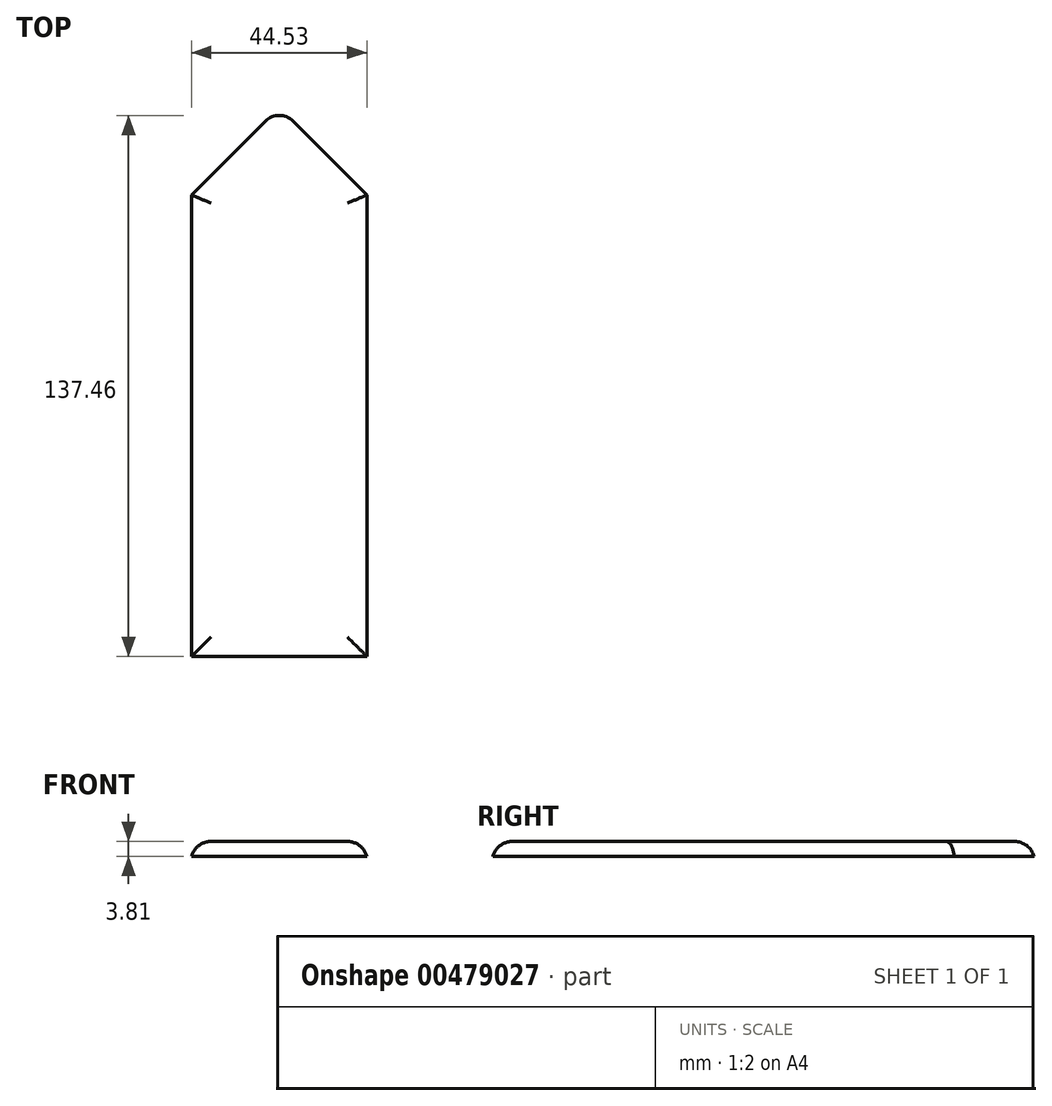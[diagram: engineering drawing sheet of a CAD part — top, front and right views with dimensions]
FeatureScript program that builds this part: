
annotation { "Feature Type Name" : "Feature", "Feature Type Description" : "" }
export const myFeature = defineFeature(function(context is Context, id is Id, definition is map)
    precondition{}
    {
        {
            var Q0;
            Q0=qCreatedBy(makeId("Top.planeOp"),FACE);
            var sketch = newSketch(context, id + "F0", { "sketchPlane" : qUnion([Q0])});
            skLineSegment(sketch, "E0.bottom", {"start": v(0, -74.1) * mm, "end": v(-44.53, -74.1) * mm});
            skLineSegment(sketch, "E0.top", {"start": v(0, 65.49) * mm, "end": v(-44.53, 65.49) * mm});
            skLineSegment(sketch, "E0.left", {"start": v(0, -74.1) * mm, "end": v(0, 65.49) * mm});
            skLineSegment(sketch, "E0.right", {"start": v(-44.53, -74.1) * mm, "end": v(-44.53, 65.49) * mm});
            skSolve(sketch);
        }
        {
            var Q0;
            Q0=makeQuery(id+"F0.imprint","IMPRINT",FACE,{"disambiguationData":[TD([[makeQuery(id+"F0.imprint","IMPRINT",EDGE,{"derivedFrom":sQuery(id+"F0.wireOp",EDGE,"E0.bottom")}),-1.0]])]});
            extrude(context, id + "F1", {"entities" : qUnion([Q0]), "depth" : 3.8 * mm});
        }
        {
            var Q0;
            Q0=makeQuery(id+"F1.opExtrude","SWEPT_EDGE",EDGE,{"disambiguationData":[OSD([sQuery(id+"F0.wireOp",EDGE,"E0.top"),sQuery(id+"F0.wireOp",EDGE,"E0.right")])]});
            chamfer(context, id + "F2", {"entities" : qUnion([Q0]), "width" : 22.35 * mm, "tangentPropagation" : true});
        }
        {
            var Q0;
            Q0=makeQuery(id+"F1.opExtrude","SWEPT_EDGE",EDGE,{"disambiguationData":[OSD([sQuery(id+"F0.wireOp",EDGE,"E0.top"),sQuery(id+"F0.wireOp",EDGE,"E0.left")])]});
            chamfer(context, id + "F3", {"entities" : qUnion([Q0]), "width" : 22.35 * mm, "tangentPropagation" : true});
        }
        {
            var Q0;
            Q0=makeQuery(id+"F1.opExtrude","CAP_FACE",FACE,{"disambiguationData":[OSD([sQuery(id+"F0.wireOp",EDGE,"E0.bottom"),sQuery(id+"F0.wireOp",EDGE,"E0.top"),sQuery(id+"F0.wireOp",EDGE,"E0.left"),sQuery(id+"F0.wireOp",EDGE,"E0.right")])],"isStart":false});
            fillet(context, id + "F4", {"entities" : qUnion([Q0]), "radius" : 5.08 * mm, "tangentPropagation" : true, "allowEdgeOverflow" : false});
        }
        {
            var Q0;
            {var subQ0=sQuery(id+"F0.wireOp",EDGE,"E0.right");var subQ1=sQuery(id+"F0.wireOp",EDGE,"E0.left");var subQ2=sQuery(id+"F0.wireOp",EDGE,"E0.top");var subQ3=makeQuery(id+"F1.opExtrude","CAP_FACE",FACE,{"disambiguationData":[OSD([sQuery(id+"F0.wireOp",EDGE,"E0.bottom"),subQ2,subQ1,subQ0])],"isStart":false});Q0=makeQuery(id+"F4.opFillet","BLEND_EDGE",EDGE,{"blendedFrom":[makeQuery(id+"F3.opChamfer","BLEND_EDGE",EDGE,{"blendedFrom":[makeQuery(id+"F1.opExtrude","SWEPT_EDGE",EDGE,{"disambiguationData":[OSD([subQ2,subQ1])]}),subQ3],"blendedInto":[subQ3]}),makeQuery(id+"F2.opChamfer","BLEND_EDGE",EDGE,{"blendedFrom":[makeQuery(id+"F1.opExtrude","SWEPT_EDGE",EDGE,{"disambiguationData":[OSD([subQ2,subQ0])]}),subQ3],"blendedInto":[subQ3]})],"blendedInto":[]});}
            fillet(context, id + "F5", {"entities" : qUnion([Q0]), "radius" : 5.08 * mm, "tangentPropagation" : true, "allowEdgeOverflow" : false});
        }
    });
